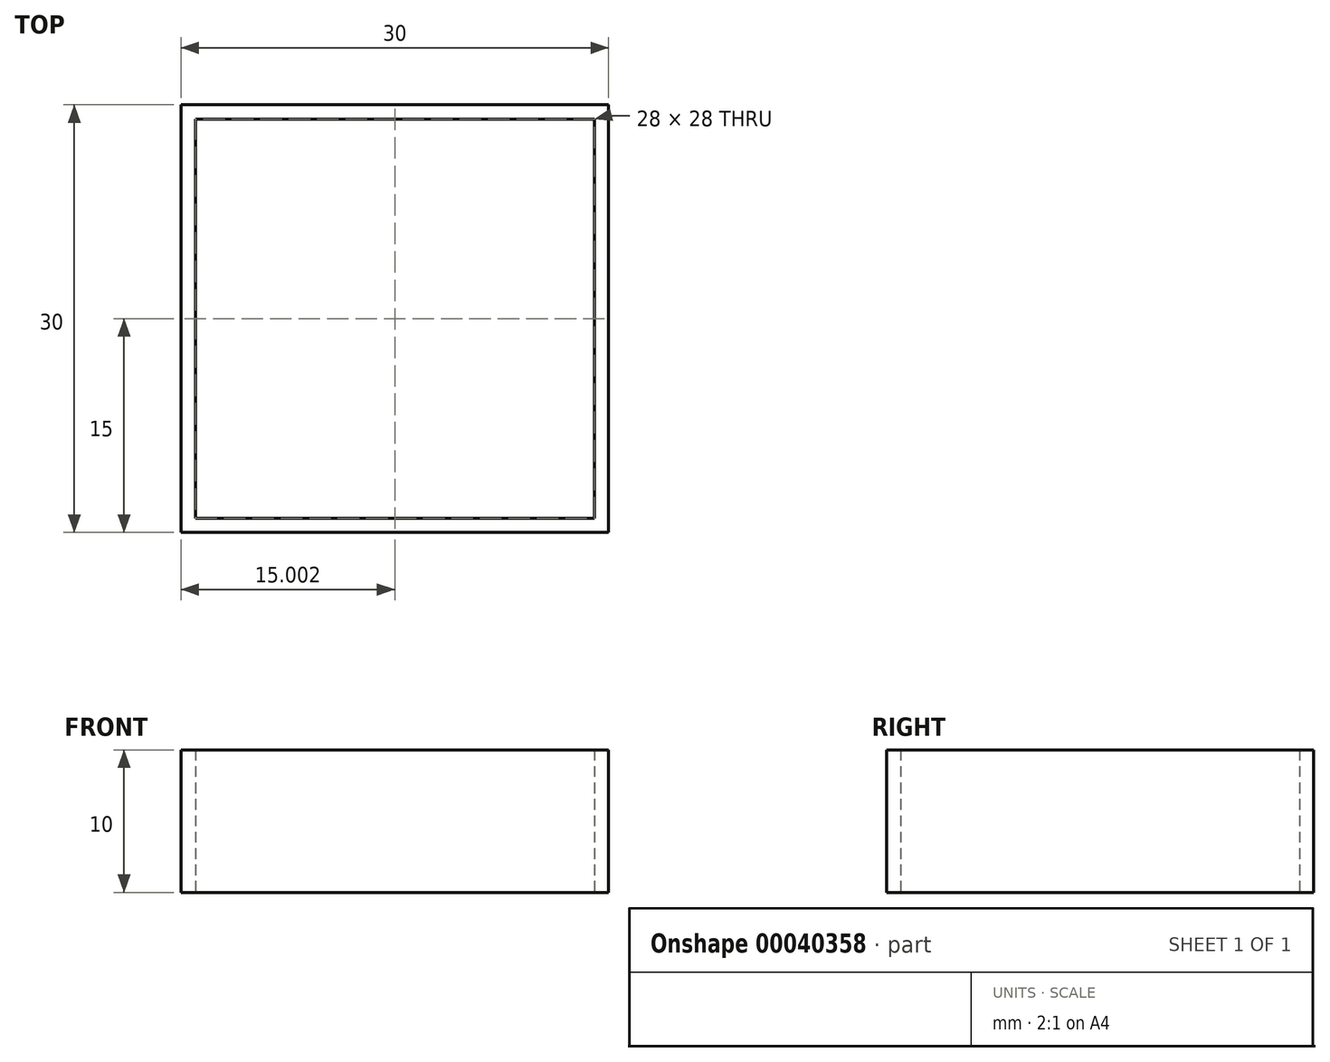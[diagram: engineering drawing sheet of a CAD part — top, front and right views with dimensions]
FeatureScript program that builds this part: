
annotation { "Feature Type Name" : "Feature", "Feature Type Description" : "" }
export const myFeature = defineFeature(function(context is Context, id is Id, definition is map)
    precondition{}
    {
        {
            var Q0;
            Q0=qCreatedBy(makeId("Top.planeOp"),FACE);
            var sketch = newSketch(context, id + "F0", { "sketchPlane" : qUnion([Q0])});
            skLineSegment(sketch, "E0.rect.bottom", {"start": v(16.1, -14) * mm, "end": v(-11.9, -14) * mm});
            skLineSegment(sketch, "E0.rect.top", {"start": v(16.1, 14) * mm, "end": v(-11.9, 14) * mm});
            skLineSegment(sketch, "E0.rect.left", {"start": v(16.1, -14) * mm, "end": v(16.1, 14) * mm});
            skLineSegment(sketch, "E0.rect.right", {"start": v(-11.9, -14) * mm, "end": v(-11.9, 14) * mm});
            skPoint(sketch, "E0.rect.middle", {"position": v(2.1, 0) * mm});
            skLineSegment(sketch, "E1.rect.bottom", {"start": v(17.1, -15) * mm, "end": v(-12.9, -15) * mm});
            skLineSegment(sketch, "E1.rect.top", {"start": v(17.1, 15) * mm, "end": v(-12.9, 15) * mm});
            skLineSegment(sketch, "E1.rect.left", {"start": v(17.1, -15) * mm, "end": v(17.1, 15) * mm});
            skLineSegment(sketch, "E1.rect.right", {"start": v(-12.9, -15) * mm, "end": v(-12.9, 15) * mm});
            skSolve(sketch);
        }
        {
            var Q0;
            Q0 = qSketchRegion(id + "F0", true);
            extrude(context, id + "F1", {"entities" : qUnion([Q0]), "depth" : 10 * mm});
        }
    });
